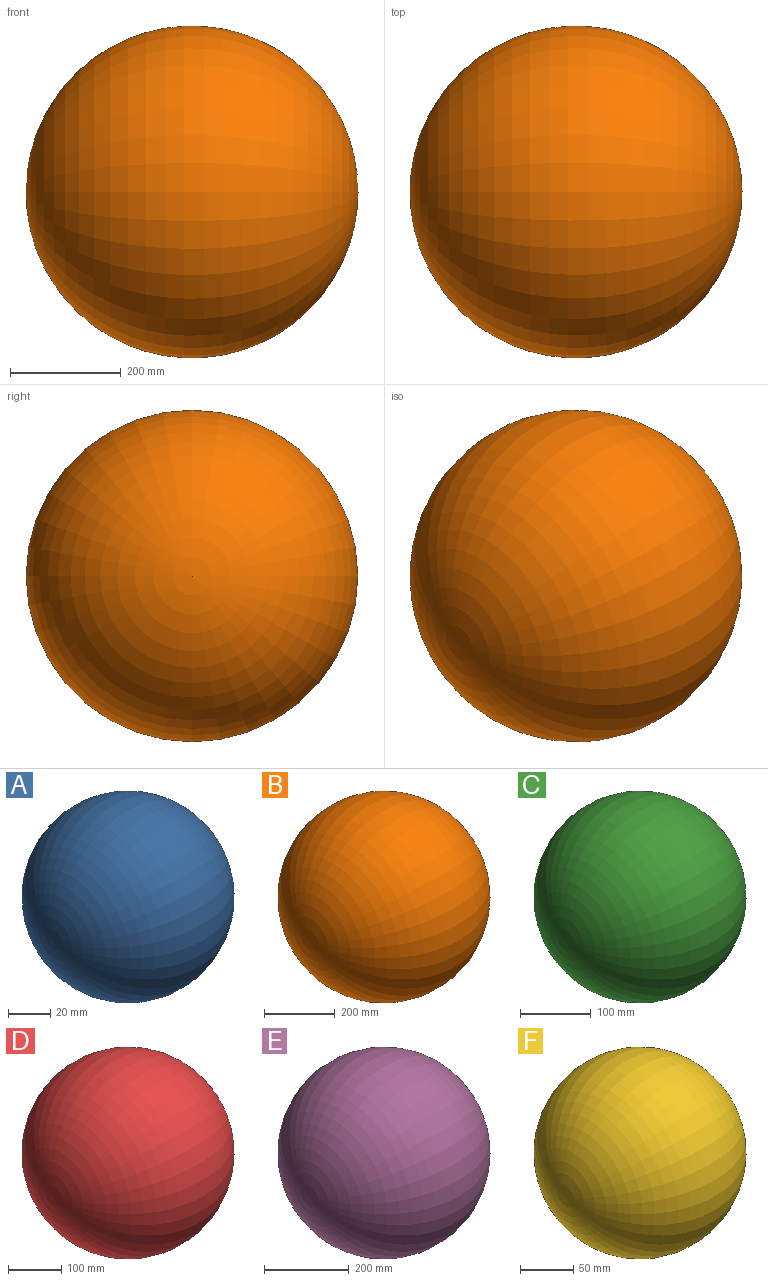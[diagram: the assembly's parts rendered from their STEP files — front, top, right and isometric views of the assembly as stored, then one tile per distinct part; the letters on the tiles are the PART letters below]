
ASSEMBLY  parts=6 mates=5
PART A: 2 faces, bbox 100x90x95 mm
  f0: torus R=0mm, axis (-1,0,0), area 31415.9mm2
  f1: sphere r=45mm, area 25446.9mm2
PART B: 2 faces, bbox 600x590x595 mm
  f0: torus R=0mm, axis (-1,0,0), area 1130973mm2
  f1: sphere r=295mm, area 1093588.4mm2
PART C: 2 faces, bbox 300x290x295 mm
  f0: torus R=0mm, axis (-1,0,0), area 282743.2mm2
  f1: sphere r=145mm, area 264207.9mm2
PART D: 2 faces, bbox 400x390x395 mm
  f0: torus R=0mm, axis (-1,0,0), area 502654.6mm2
  f1: sphere r=195mm, area 477836.2mm2
PART E: 2 faces, bbox 500x490x495 mm
  f0: torus R=0mm, axis (-1,0,0), area 785397.9mm2
  f1: sphere r=245mm, area 754296.4mm2
PART F: 2 faces, bbox 200x190x195 mm
  f0: torus R=0mm, axis (-1,0,0), area 125663.6mm2
  f1: sphere r=95mm, area 113411.5mm2
PLACE A t=(0.23,0.13,0)mm
PLACE B t=(0.23,0.13,0)mm
PLACE C t=(0.23,0.13,0)mm
PLACE D t=(0.23,0.13,0)mm
PLACE E t=(0.23,0.13,0)mm
PLACE F t=(0.23,0.13,0)mm
MATE fastened A.f0 <-> C.f0  axis (-1,0,0) through (0.23,0.13,0)mm
MATE fastened A.f0 <-> E.f0  axis (-1,0,0) through (0.23,0.13,0)mm
MATE fastened A.f0 <-> F.f0  axis (-1,0,0) through (0.23,0.13,0)mm
MATE fastened A.f0 <-> D.f0  axis (-1,0,0) through (0.23,0.13,0)mm
MATE fastened A.f0 <-> B.f0  axis (-1,0,0) through (0.23,0.13,0)mm
